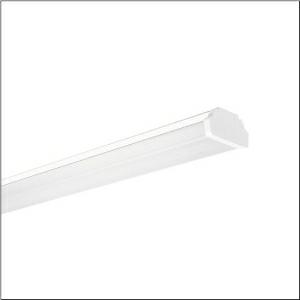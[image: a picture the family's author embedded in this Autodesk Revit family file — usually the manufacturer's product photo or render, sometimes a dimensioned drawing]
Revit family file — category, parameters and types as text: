
# Revit family: dus_r__31_mo_53bd812d2v6085_5279
name_source: partatom
category: Lighting Fixtures
units: mm (PartAtom-declared; Revit-internal decimal feet)

## family parameters
Cut with Voids When Loaded = No
Host = Face
Light Source = No
Part Type = Normal
Room Calculation Point = No
Round Connector Dimension = Use Diameter
Shared = No

## types (1)
- --- (1 x LED, 8960 lm, 61.8 W, 6500K)
    Apparent Load = 62 VA
    CIE Flux Codes = 47 80 95 92 100
    Color Rendering = 80
    Color Temperature = 6500K
    Default Elevation = 1800 mm
    Description = DUS® 31 MOluminaire insert, length: 1.535mm, width: 81mm, height: 90mm, LED rated luminous flux: 8.960lm, light colour: 865, control gear: DALI 2, control gear: ECG DALI, with plug, 5-pole, with phase selection, mains connection: 220..240V, AC, 50/60Hz, primary optical cover: cover, of PMMA, light emission: direct distribution, primary light characteristic: symmetric, protection rating (complete): IP20, protection rating (LED compartment): IP50, insulation class (complete): insulation class I (protective earthing), certification: CE, ENEC, VDE, permissible ambient temperature for indoor applications: -25..+30°C, corresponds to IFS (International Featured Standards) requirements for safety and quality in the food industry, reducing of maximum allowable ambient temperature of 5°C with ceiling mounting, packaging unit: 1 piece
    Height = 95 mm
    Lamp = 1 x LED
    Lamp Light Flux = 8960 lm
    Lamp Power = 61.8 W
    Lamp count = 1
    Length = 1535 mm
    Luminous efficacy = 145 lm/W
    Manufacturer = Siteco
    ModVariant = No
    Model = 53BD812D2V6085
    Mounting Place = Ceiling
    Mounting Type = Pendant
    Number of Poles = 1
    OnlyDefault = Yes
    Power Factor = 1
    Product Name = DUS® 31 MO
    Product group = luminaire insert
    ProductGroupID = 902
    Protection Class = Protection class I
    Protection Degree = IP 20
    RLX_Detail_Level = 1
    RlxData = <blob elided: 41773 chars, md5=b7545822>
    Socket = socket
    Standby Power = 0 W
    System Light Flux = 8960 lm
    System Power = 62 W
    Type Comments = factory setting: luminous flux: 100 % | dim-lin: 254 | 500 mA
    Type Image = l_1003451.jpg
    URL = http://relux.com
    VarID = @adj_117333
    Voltage = 0 V
    Weight = 0.00 kg
    Width = 81 mm

## geometry (parser evidence)
native form markers: Blend x4, Sweep x13
no freeform markers — native parametric forms only
